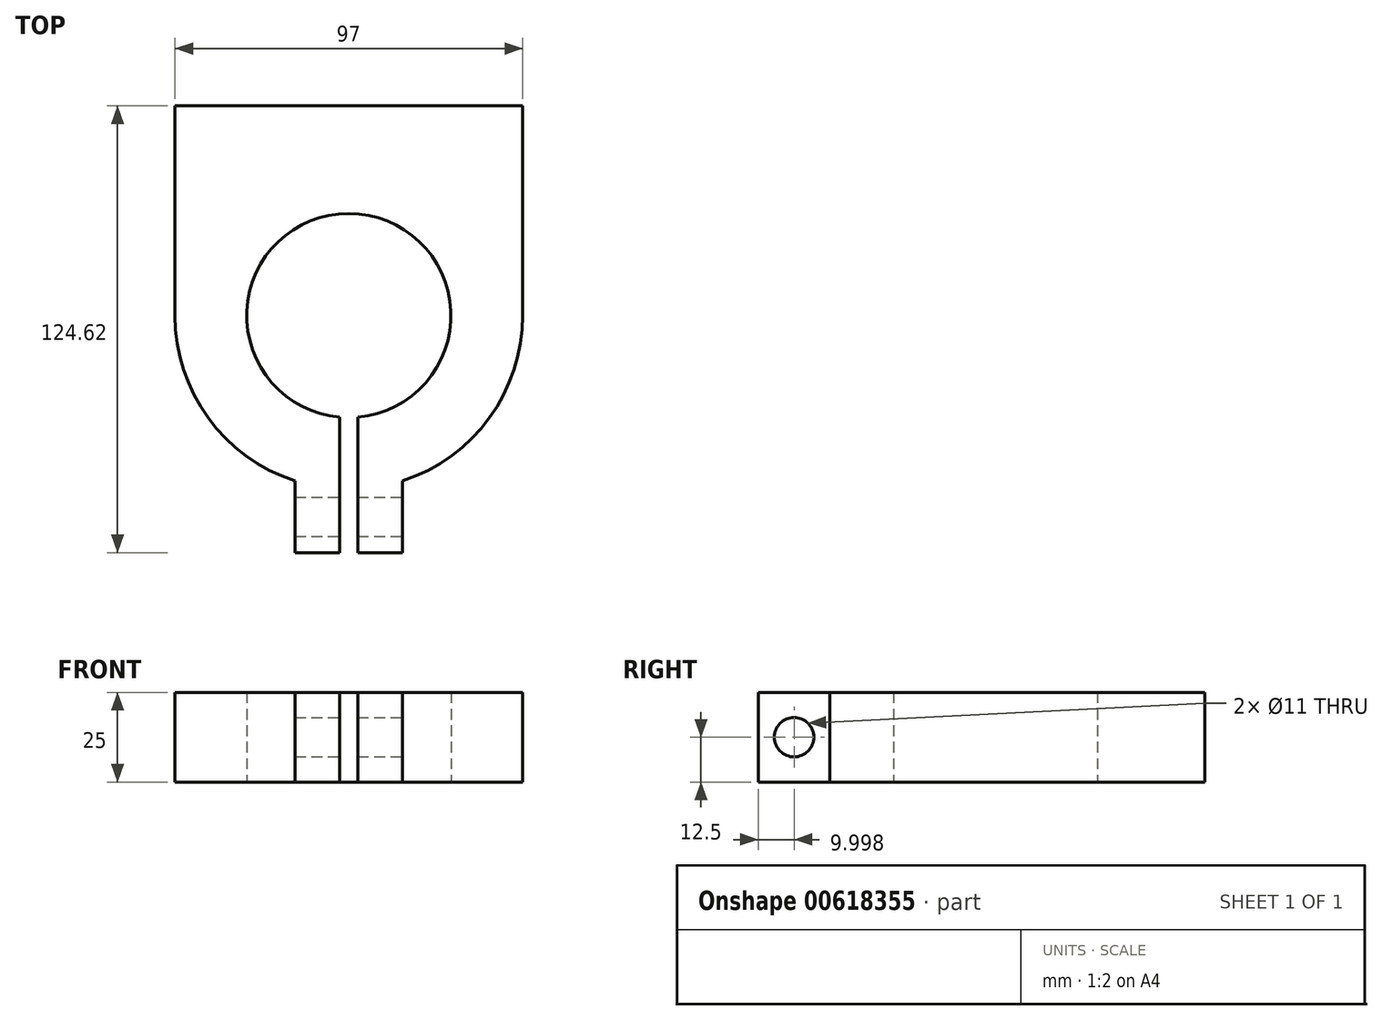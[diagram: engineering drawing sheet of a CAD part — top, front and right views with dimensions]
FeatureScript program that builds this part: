
annotation { "Feature Type Name" : "Feature", "Feature Type Description" : "" }
export const myFeature = defineFeature(function(context is Context, id is Id, definition is map)
    precondition{}
    {
        {
            var Q0;
            Q0=qCreatedBy(makeId("Top.planeOp"),FACE);
            var sketch = newSketch(context, id + "F0", { "sketchPlane" : qUnion([Q0])});
            skArc(sketch, "E0", {"start": v(2.5, -28.4) * mm, "mid": v(0, 28.5) * mm, "end": v(-2.5, -28.4) * mm});
            skArc(sketch, "E1", {"start": v(15, -46.12) * mm, "mid": v(0, 48.5) * mm, "end": v(-15, -46.12) * mm});
            skLineSegment(sketch, "E2", {"start": v(0, 93.6) * mm, "end": v(0, -93.6) * mm, "construction": true});
            skLineSegment(sketch, "E3", {"start": v(-118.74, 0) * mm, "end": v(-28.5, 0) * mm, "construction": true});
            skLineSegment(sketch, "E4.bottom", {"start": v(-15, -66.12) * mm, "end": v(-2.5, -66.12) * mm});
            skLineSegment(sketch, "E4.left", {"start": v(-15, -66.12) * mm, "end": v(-15, -46.12) * mm});
            skLineSegment(sketch, "E4.right", {"start": v(15, -66.12) * mm, "end": v(15, -46.12) * mm});
            skLineSegment(sketch, "E5.left", {"start": v(-2.5, -28.4) * mm, "end": v(-2.5, -66.12) * mm});
            skLineSegment(sketch, "E5.right", {"start": v(2.5, -28.4) * mm, "end": v(2.5, -66.12) * mm});
            skLineSegment(sketch, "E6.trimOffspring", {"start": v(2.5, -66.12) * mm, "end": v(15, -66.12) * mm});
            skPoint(sketch, "E7.endSnap0", {"position": v(-15, -56.12) * mm});
            skLineSegment(sketch, "E8", {"start": v(0, -68.59) * mm, "end": v(-68.59, 0) * mm, "construction": true});
            skLineSegment(sketch, "E9", {"start": v(-99.93, -99.93) * mm, "end": v(97.82, 97.82) * mm, "construction": true});
            skLineSegment(sketch, "E10.bottom", {"start": v(-48.5, 58.5) * mm, "end": v(48.5, 58.5) * mm});
            skLineSegment(sketch, "E10.top", {"start": v(-48.5, 0) * mm, "end": v(-28.5, 0) * mm});
            skLineSegment(sketch, "E10.left", {"start": v(-48.5, 58.5) * mm, "end": v(-48.5, 0) * mm});
            skLineSegment(sketch, "E10.right", {"start": v(48.5, 58.5) * mm, "end": v(48.5, 0) * mm});
            skLineSegment(sketch, "E11.trimOffspring", {"start": v(28.5, 0) * mm, "end": v(118.74, 0) * mm, "construction": true});
            skLineSegment(sketch, "E12.trimOffspring", {"start": v(28.5, 0) * mm, "end": v(48.5, 0) * mm});
            skSolve(sketch);
        }
        {
            var Q0;
            Q0 = qSketchRegion(id + "F0", true);
            extrude(context, id + "F1", {"entities" : qUnion([Q0]), "endBound" : BoundingType.SYMMETRIC, "depth" : 25 * mm, "offsetDistance" : 25 * mm});
        }
        {
            var Q0;
            Q0=makeQuery(id+"F1.opExtrude","SWEPT_FACE",FACE,{"disambiguationData":[OSD([sQuery(id+"F0.wireOp",EDGE,"E4.right")])]});
            var sketch = newSketch(context, id + "F2", { "sketchPlane" : qUnion([Q0])});
            skLineSegment(sketch, "E13.0.0", {"start": v(-66.12, -12.5) * mm, "end": v(-46.12, -12.5) * mm});
            skLineSegment(sketch, "E13.0.1", {"start": v(-46.12, -12.5) * mm, "end": v(-46.12, 12.5) * mm});
            skLineSegment(sketch, "E13.0.2", {"start": v(-46.12, 12.5) * mm, "end": v(-66.12, 12.5) * mm});
            skLineSegment(sketch, "E13.0.3", {"start": v(-66.12, 12.5) * mm, "end": v(-66.12, -12.5) * mm});
            skLineSegment(sketch, "E14", {"start": v(-56.12, 12.5) * mm, "end": v(-56.12, -12.5) * mm, "construction": true});
            skLineSegment(sketch, "E15", {"start": v(-66.12, 0) * mm, "end": v(-46.12, 0) * mm, "construction": true});
            skPoint(sketch, "E16", {"position": v(-56.12, 0) * mm});
            skSolve(sketch);
        }
        {
            var Q0;
            Q0=sQuery(id+"F2.wireOp",VERTEX,"E16");
            var Q1;
            Q1=makeQuery(id+"F1.opExtrude","SWEPT_BODY",BODY,{"disambiguationData":[OSD([sQuery(id+"F0.wireOp",EDGE,"E0"),sQuery(id+"F0.wireOp",EDGE,"E1"),sQuery(id+"F0.wireOp",EDGE,"E4.bottom"),sQuery(id+"F0.wireOp",EDGE,"E4.left"),sQuery(id+"F0.wireOp",EDGE,"E4.right"),sQuery(id+"F0.wireOp",EDGE,"E5.left"),sQuery(id+"F0.wireOp",EDGE,"E5.right"),sQuery(id+"F0.wireOp",EDGE,"E6.trimOffspring"),sQuery(id+"F0.wireOp",EDGE,"E10.bottom"),sQuery(id+"F0.wireOp",EDGE,"E10.left"),sQuery(id+"F0.wireOp",EDGE,"E10.right")])]});
            hole(context, id + "F3", {"style" : HoleStyle.SIMPLE, "endStyle" : HoleEndStyle.THROUGH, "standardTappedOrClearance" : lookupTablePath({ "standard" : "ISO", "fit" : "Normal", "size" : "M10", "type" : "Clearance" }), "standardBlindInLast" : lookupTablePath({ "fit" : "Standard", "standard" : "ISO", "size" : "M10", "type" : "Clearance" }), "holeDiameter" : 11 * mm, "majorDiameter" : 5 * mm, "isTappedThrough" : true, "tappedDepth" : 12 * mm, "tapClearance" : 3, "locations" : qUnion([Q0]), "scope" : qUnion([Q1])});
        }
    });
